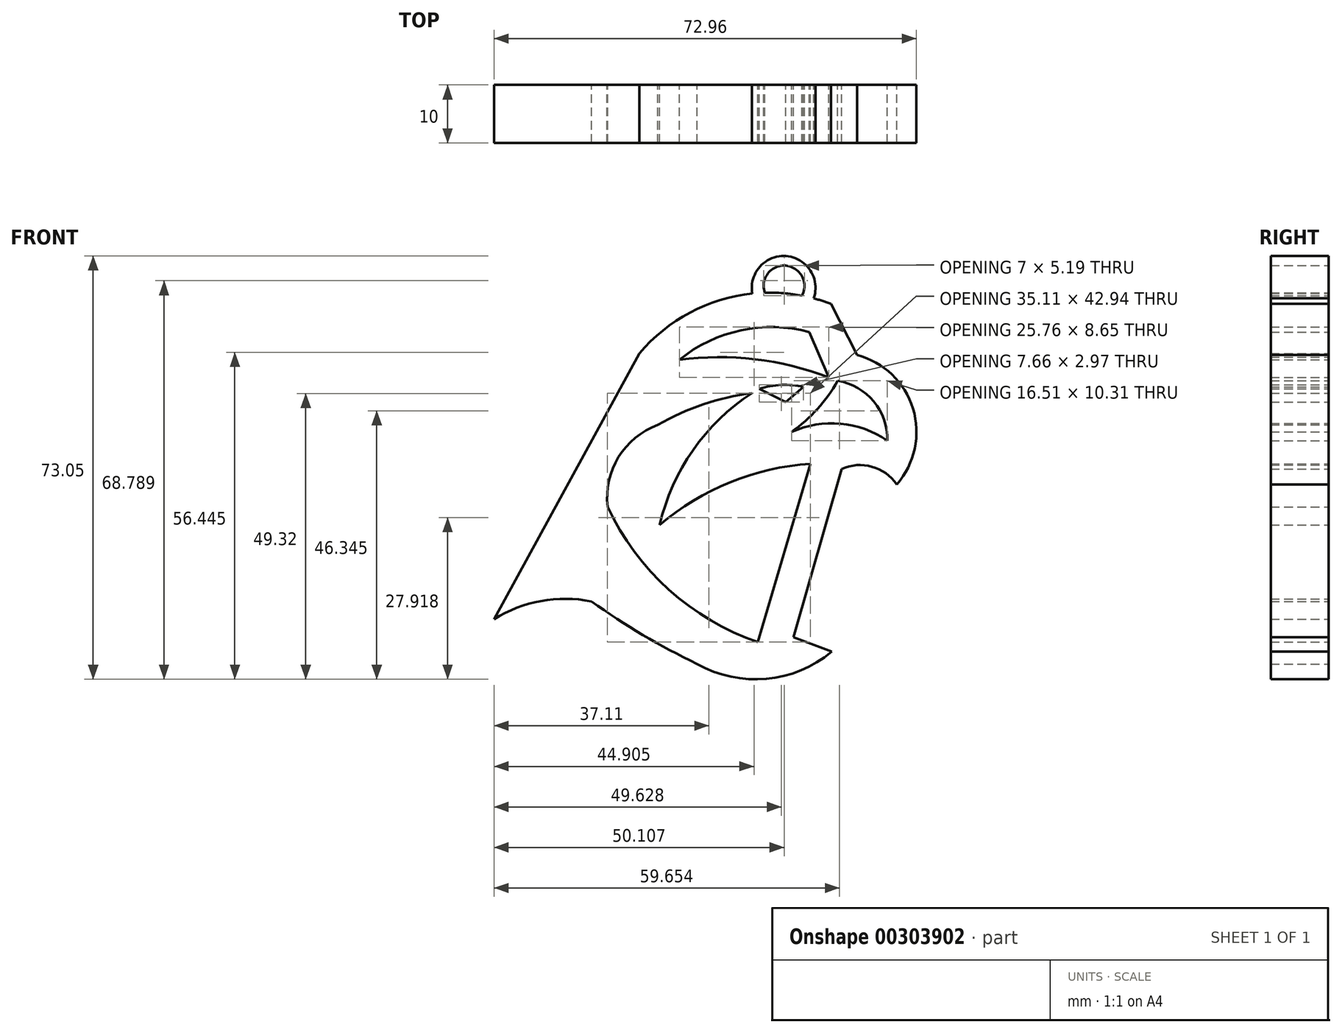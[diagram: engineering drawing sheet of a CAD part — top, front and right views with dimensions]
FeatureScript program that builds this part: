
annotation { "Feature Type Name" : "Feature", "Feature Type Description" : "" }
export const myFeature = defineFeature(function(context is Context, id is Id, definition is map)
    precondition{}
    {
        {
            var Q0;
            Q0=qCreatedBy(makeId("Front.planeOp"),FACE);
            var sketch = newSketch(context, id + "F0", { "sketchPlane" : qUnion([Q0])});
            skArc(sketch, "E0", {"start": v(18.83, 30.15) * mm, "mid": v(0.92, 31.15) * mm, "end": v(-14.26, 21.6) * mm});
            skLineSegment(sketch, "E1", {"start": v(-14.26, 21.6) * mm, "end": v(-39.36, -24.26) * mm});
            skArc(sketch, "E2", {"start": v(-22.53, -21.17) * mm, "mid": v(-31.24, -21.11) * mm, "end": v(-39.36, -24.26) * mm});
            skArc(sketch, "E3", {"start": v(-22.53, -21.17) * mm, "mid": v(-13.65, -26.96) * mm, "end": v(-4.3, -31.97) * mm});
            skArc(sketch, "E4", {"start": v(-4.3, -31.97) * mm, "mid": v(7.66, -34.54) * mm, "end": v(18.97, -29.87) * mm});
            skLineSegment(sketch, "E5", {"start": v(18.97, -29.87) * mm, "end": v(12.38, -27.34) * mm});
            skLineSegment(sketch, "E6", {"start": v(12.38, -27.34) * mm, "end": v(20.65, 1.68) * mm});
            skArc(sketch, "E7", {"start": v(30.19, -0.98) * mm, "mid": v(25.9, 2.05) * mm, "end": v(20.65, 1.68) * mm});
            skArc(sketch, "E8", {"start": v(30.19, -0.98) * mm, "mid": v(33, 12.09) * mm, "end": v(23.32, 21.31) * mm});
            skLineSegment(sketch, "E9", {"start": v(18.83, 30.15) * mm, "end": v(23.32, 21.31) * mm});
            skArc(sketch, "E10", {"start": v(28.55, 6.56) * mm, "mid": v(26.2, 13.32) * mm, "end": v(20, 16.87) * mm});
            skArc(sketch, "E11", {"start": v(28.55, 6.56) * mm, "mid": v(20.5, 9.48) * mm, "end": v(12.04, 8.06) * mm});
            skArc(sketch, "E12", {"start": v(12.04, 8.06) * mm, "mid": v(16.5, 12.03) * mm, "end": v(20, 16.87) * mm});
            skArc(sketch, "E13", {"start": v(14.1, 15.84) * mm, "mid": v(10.25, 16.17) * mm, "end": v(6.44, 15.52) * mm});
            skLineSegment(sketch, "E14", {"start": v(14.1, 15.84) * mm, "end": v(11.01, 13.2) * mm});
            skLineSegment(sketch, "E15", {"start": v(11.01, 13.2) * mm, "end": v(6.44, 15.52) * mm});
            skArc(sketch, "E16", {"start": v(5.15, 14.76) * mm, "mid": v(-4.99, 4.92) * mm, "end": v(-10.75, -7.98) * mm});
            skArc(sketch, "E17", {"start": v(15.3, 2.57) * mm, "mid": v(1.43, -0.62) * mm, "end": v(-10.75, -7.98) * mm});
            skLineSegment(sketch, "E18", {"start": v(15.3, 2.57) * mm, "end": v(6.23, -28.18) * mm});
            skArc(sketch, "E19", {"start": v(-19.73, -4.86) * mm, "mid": v(-9.14, -19.18) * mm, "end": v(6.23, -28.18) * mm});
            skArc(sketch, "E20", {"start": v(-11.04, 9.3) * mm, "mid": v(-17.84, 3.72) * mm, "end": v(-19.73, -4.86) * mm});
            skArc(sketch, "E21", {"start": v(5.15, 14.76) * mm, "mid": v(-3.2, 12.8) * mm, "end": v(-11.04, 9.3) * mm});
            skArc(sketch, "E22", {"start": v(18.43, 17.49) * mm, "mid": v(5.73, 20.59) * mm, "end": v(-7.34, 20.51) * mm});
            skArc(sketch, "E23", {"start": v(15.1, 25.3) * mm, "mid": v(3.31, 25.6) * mm, "end": v(-7.34, 20.51) * mm});
            skLineSegment(sketch, "E24", {"start": v(15.1, 25.3) * mm, "end": v(18.43, 17.49) * mm});
            skArc(sketch, "E25", {"start": v(15.86, 31.1) * mm, "mid": v(11.09, 38.4) * mm, "end": v(5.25, 31.93) * mm});
            skArc(sketch, "E26", {"start": v(13.83, 31.56) * mm, "mid": v(11, 36.75) * mm, "end": v(7.4, 32.07) * mm});
            skSolve(sketch);
        }
        {
            var Q0;
            Q0 = qSketchRegion(id + "F0", true);
            extrude(context, id + "F1", {"entities" : qUnion([Q0]), "depth" : 10 * mm});
        }
        {
            var Q0;
            Q0 = qSketchRegion(id + "F0", true);
            extrude(context, id + "F2", {"entities" : qUnion([Q0]), "operationType" : NewBodyOperationType.ADD, "depth" : 3 * mm});
        }
        {
            var Q0;
            Q0 = qSketchRegion(id + "F0", true);
            extrude(context, id + "F3", {"entities" : qUnion([Q0]), "operationType" : NewBodyOperationType.ADD, "depth" : 3 * mm});
        }
        {
            var Q0;
            Q0 = qSketchRegion(id + "F0", true);
            extrude(context, id + "F4", {"entities" : qUnion([Q0]), "operationType" : NewBodyOperationType.ADD, "depth" : 3 * mm});
        }
        {
            var Q0;
            Q0 = qSketchRegion(id + "F0", true);
            extrude(context, id + "F5", {"entities" : qUnion([Q0]), "operationType" : NewBodyOperationType.ADD, "depth" : 3 * mm});
        }
    });
